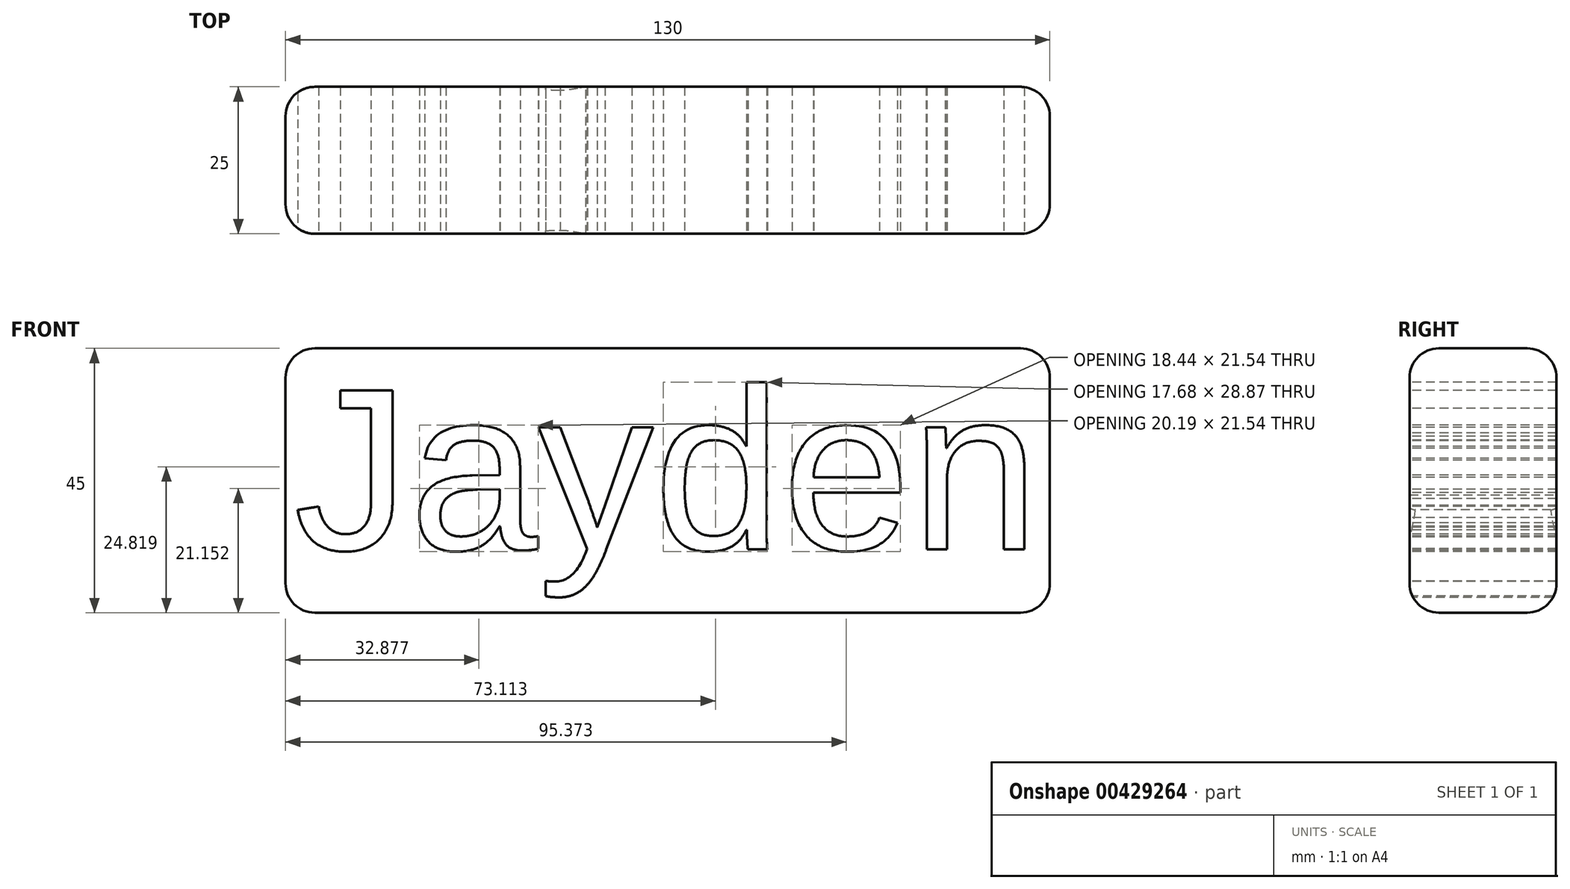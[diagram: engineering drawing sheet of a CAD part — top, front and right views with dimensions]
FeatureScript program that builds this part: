
annotation { "Feature Type Name" : "Feature", "Feature Type Description" : "" }
export const myFeature = defineFeature(function(context is Context, id is Id, definition is map)
    precondition{}
    {
        {
            var Q0;
            Q0=qCreatedBy(makeId("Front.planeOp"),FACE);
            var sketch = newSketch(context, id + "F0", { "sketchPlane" : qUnion([Q0])});
            skLineSegment(sketch, "E0.bottom", {"start": v(0, 0) * mm, "end": v(130, 0) * mm});
            skLineSegment(sketch, "E0.top", {"start": v(0, 45) * mm, "end": v(130, 45) * mm});
            skLineSegment(sketch, "E0.left", {"start": v(0, 0) * mm, "end": v(0, 45) * mm});
            skLineSegment(sketch, "E0.right", {"start": v(130, 0) * mm, "end": v(130, 45) * mm});
            skSolve(sketch);
        }
        {
            var Q0;
            Q0=makeQuery(id+"F0.imprint","IMPRINT",FACE,{"disambiguationData":[TD([[makeQuery(id+"F0.imprint","IMPRINT",EDGE,{"derivedFrom":sQuery(id+"F0.wireOp",EDGE,"E0.bottom")}),1.0]])]});
            extrude(context, id + "F1", {"entities" : qUnion([Q0]), "oppositeDirection" : true, "depth" : 25 * mm});
        }
        {
            var Q0;
            Q0=makeQuery(id+"F1.opExtrude","CAP_FACE",FACE,{"disambiguationData":[OSD([sQuery(id+"F0.wireOp",EDGE,"E0.bottom"),sQuery(id+"F0.wireOp",EDGE,"E0.top"),sQuery(id+"F0.wireOp",EDGE,"E0.left"),sQuery(id+"F0.wireOp",EDGE,"E0.right")])],"isStart":true});
            var sketch = newSketch(context, id + "F2", { "sketchPlane" : qUnion([Q0])});
            skText(sketch, "E1", { "text": "Jayden", "fontName": "Arimo-Regular.ttf"});
            const initialGuessF2  = {"E1": [0.00146, 0.01077, 1, 0, 0.0283]};
            skSetInitialGuess(sketch, initialGuessF2);
            skSolve(sketch);
        }
        {
            var Q0;
            Q0 = qSketchRegion(id + "F2", true);
            extrude(context, id + "F3", {"entities" : qUnion([Q0]), "operationType" : NewBodyOperationType.REMOVE, "oppositeDirection" : true, "depth" : 25 * mm});
        }
        {
            var Q0;
            Q0=makeQuery(id+"F1.opExtrude","SWEPT_FACE",FACE,{"disambiguationData":[OSD([sQuery(id+"F0.wireOp",EDGE,"E0.right")])]});
            var Q1;
            Q1=makeQuery(id+"F1.opExtrude","SWEPT_FACE",FACE,{"disambiguationData":[OSD([sQuery(id+"F0.wireOp",EDGE,"E0.top")])]});
            var Q2;
            Q2=makeQuery(id+"F1.opExtrude","SWEPT_FACE",FACE,{"disambiguationData":[OSD([sQuery(id+"F0.wireOp",EDGE,"E0.left")])]});
            var Q3;
            Q3=makeQuery(id+"F1.opExtrude","SWEPT_FACE",FACE,{"disambiguationData":[OSD([sQuery(id+"F0.wireOp",EDGE,"E0.bottom")])]});
            fillet(context, id + "F4", {"entities" : qUnion([Q0, Q1, Q2, Q3]), "radius" : 5 * mm, "tangentPropagation" : true, "allowEdgeOverflow" : false});
        }
    });
